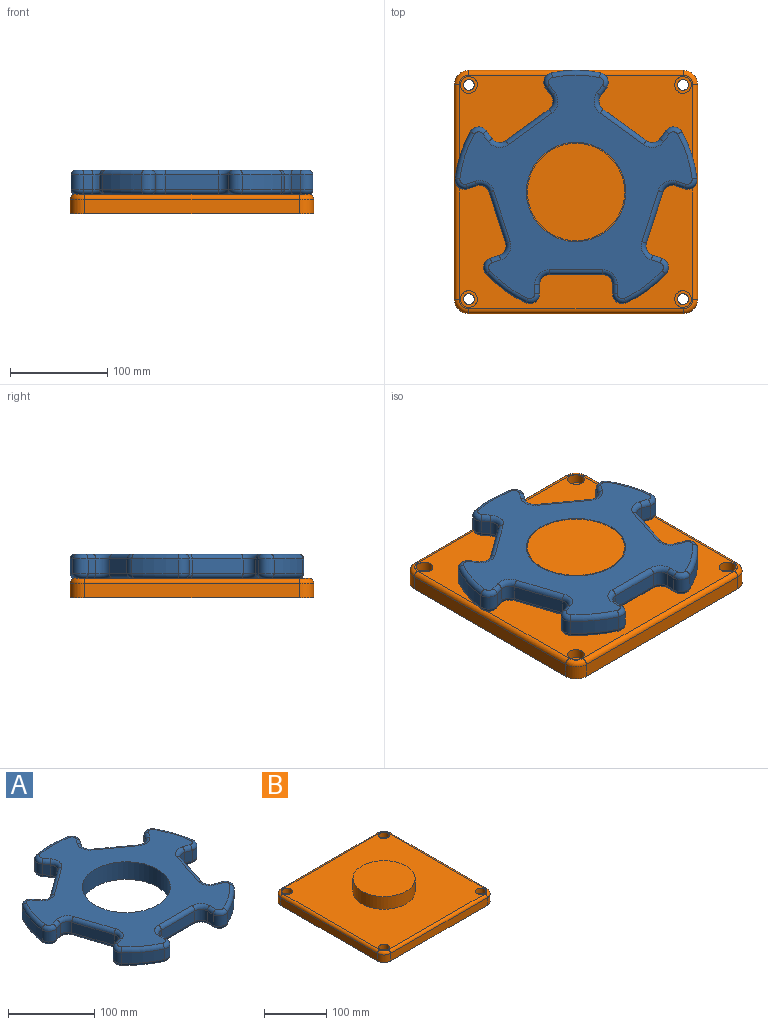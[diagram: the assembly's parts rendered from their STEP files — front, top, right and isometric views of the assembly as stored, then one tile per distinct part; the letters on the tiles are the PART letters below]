
ASSEMBLY  parts=2 mates=1
PART A: 123 faces, bbox 268.9x258.5x25 mm
  f0: plane 238.57x229.73mm, normal (0,0,1), area 21505.7mm2, adj f6,f43,f44,f45,f46,f47,f48,f49
  f1: plane 238.57x229.73mm, normal (0,0,-1), area 21505.7mm2, adj f6,f83,f84,f85,f86,f87,f88,f89
  f2: cylinder r=125mm len=40.68mm, axis (0,0,-1), area 759.5mm2, adj f13,f42,f51,f91
  f3: cylinder r=125mm len=47.82mm, axis (0,0,-1), area 759.5mm2, adj f35,f41,f67,f107
  f4: cylinder r=125mm len=50.29mm, axis (0,0,-1), area 759.5mm2, adj f28,f34,f82,f122
  f5: cylinder r=125mm len=47.82mm, axis (0,0,-1), area 759.5mm2, adj f21,f27,f66,f106
  f6: cylinder r=51mm len=102mm, axis (0,0,-1), area 8011.1mm2, adj f0,f1
  f7: cylinder r=125mm len=40.68mm, axis (0,0,-1), area 759.5mm2, adj f14,f20,f50,f90
  f8: plane 15x9.73mm, normal (-1,0,0), area 146mm2, adj f11,f14,f46,f86
  f9: plane 55x15mm, normal (0,-1,0), area 825mm2, adj f11,f12,f43,f83
  f10: plane 15x9.73mm, normal (1,0,0), area 146mm2, adj f12,f13,f47,f87
  f11: cylinder r=10mm len=15mm, axis (0,0,-1), area 235.6mm2, adj f8,f9,f44,f84
  f12: cylinder r=10mm len=15mm, axis (0,0,-1), area 235.6mm2, adj f9,f10,f45,f85
  f13: cylinder r=10mm len=15mm, axis (0,0,-1), area 299.5mm2, adj f2,f10,f49,f89
  f14: cylinder r=10mm len=15mm, axis (0,0,-1), area 299.5mm2, adj f7,f8,f48,f88
  f15: plane 15x9.26mm, normal (-0.31,-0.95,0), area 146mm2, adj f18,f21,f62,f102
  f16: plane 52.31x17mm, normal (0.95,-0.31,0), area 825mm2, adj f18,f19,f58,f98
  f17: plane 15x9.26mm, normal (0.31,0.95,0), area 146mm2, adj f19,f20,f54,f94
  f18: cylinder r=10mm len=15mm, axis (0,0,-1), area 235.6mm2, adj f15,f16,f60,f100
  f19: cylinder r=10mm len=15mm, axis (0,0,-1), area 235.6mm2, adj f16,f17,f56,f96
  f20: cylinder r=10mm len=16.25mm, axis (0,0,-1), area 299.5mm2, adj f7,f17,f52,f92
  f21: cylinder r=10mm len=15mm, axis (0,0,-1), area 299.5mm2, adj f5,f15,f64,f104
  f22: plane 15x7.87mm, normal (0.81,-0.59,0), area 146mm2, adj f25,f28,f78,f118
  f23: plane 44.5x32.33mm, normal (0.59,0.81,0), area 825mm2, adj f25,f26,f74,f114
  f24: plane 15x7.87mm, normal (-0.81,0.59,0), area 146mm2, adj f26,f27,f70,f110
  f25: cylinder r=10mm len=15mm, axis (0,0,-1), area 235.6mm2, adj f22,f23,f76,f116
  f26: cylinder r=10mm len=15mm, axis (0,0,-1), area 235.6mm2, adj f23,f24,f72,f112
  f27: cylinder r=10mm len=16.78mm, axis (0,0,-1), area 299.5mm2, adj f5,f24,f68,f108
  f28: cylinder r=10mm len=15.67mm, axis (0,0,-1), area 299.5mm2, adj f4,f22,f80,f120
  f29: plane 15x7.87mm, normal (0.81,0.59,0), area 146mm2, adj f32,f35,f71,f111
  f30: plane 44.5x32.33mm, normal (-0.59,0.81,0), area 825mm2, adj f32,f33,f75,f115
  f31: plane 15x7.87mm, normal (-0.81,-0.59,0), area 146mm2, adj f33,f34,f79,f119
  f32: cylinder r=10mm len=15mm, axis (0,0,-1), area 235.6mm2, adj f29,f30,f73,f113
  f33: cylinder r=10mm len=15mm, axis (0,0,-1), area 235.6mm2, adj f30,f31,f77,f117
  f34: cylinder r=10mm len=15.67mm, axis (0,0,-1), area 299.5mm2, adj f4,f31,f81,f121
  f35: cylinder r=10mm len=16.78mm, axis (0,0,-1), area 299.5mm2, adj f3,f29,f69,f109
  f36: plane 15x9.26mm, normal (-0.31,0.95,0), area 146mm2, adj f39,f42,f55,f95
  f37: plane 52.31x17mm, normal (-0.95,-0.31,0), area 825mm2, adj f39,f40,f59,f99
  f38: plane 15x9.26mm, normal (0.31,-0.95,0), area 146mm2, adj f40,f41,f63,f103
  f39: cylinder r=10mm len=15mm, axis (0,0,-1), area 235.6mm2, adj f36,f37,f57,f97
  f40: cylinder r=10mm len=15mm, axis (0,0,-1), area 235.6mm2, adj f37,f38,f61,f101
  f41: cylinder r=10mm len=15mm, axis (0,0,-1), area 299.5mm2, adj f3,f38,f65,f105
  f42: cylinder r=10mm len=16.25mm, axis (0,0,-1), area 299.5mm2, adj f2,f36,f53,f93
  f43: cylinder r=5mm len=55mm, axis (1,0,0), area 432mm2, adj f0,f9,f44,f45
  f44: torus R=15mm, axis (0,0,1), area 145.8mm2, adj f0,f11,f43,f46
  f45: torus R=15mm, axis (0,0,1), area 145.8mm2, adj f0,f12,f43,f47
  f46: cylinder r=5mm len=9.73mm, axis (0,-1,0), area 76.4mm2, adj f0,f8,f44,f48
  f47: cylinder r=5mm len=9.73mm, axis (0,1,0), area 76.4mm2, adj f0,f10,f45,f49
  f48: torus R=5mm, axis (0,0,1), area 128.3mm2, adj f0,f14,f46,f50
  f49: torus R=5mm, axis (0,0,1), area 128.3mm2, adj f0,f13,f47,f51
  f50: torus R=120mm, axis (0,0,1), area 391.9mm2, adj f0,f7,f48,f52
  f51: torus R=120mm, axis (0,0,1), area 391.9mm2, adj f0,f2,f49,f53
  f52: torus R=5mm, axis (0,0,1), area 128.3mm2, adj f0,f20,f50,f54
  f53: torus R=5mm, axis (0,0,1), area 128.3mm2, adj f0,f42,f51,f55
  f54: cylinder r=5mm len=10.8mm, axis (-0.95,0.31,0), area 76.4mm2, adj f0,f17,f52,f56
  f55: cylinder r=5mm len=10.8mm, axis (-0.95,-0.31,0), area 76.4mm2, adj f0,f36,f53,f57
  f56: torus R=15mm, axis (0,0,1), area 145.8mm2, adj f0,f19,f54,f58
  f57: torus R=15mm, axis (0,0,1), area 145.8mm2, adj f0,f39,f55,f59
  f58: cylinder r=5mm len=53.85mm, axis (0.31,0.95,0), area 432mm2, adj f0,f16,f56,f60
  f59: cylinder r=5mm len=53.85mm, axis (0.31,-0.95,0), area 432mm2, adj f0,f37,f57,f61
  f60: torus R=15mm, axis (0,0,1), area 145.8mm2, adj f0,f18,f58,f62
  f61: torus R=15mm, axis (0,0,1), area 145.8mm2, adj f0,f40,f59,f63
  f62: cylinder r=5mm len=10.8mm, axis (0.95,-0.31,0), area 76.4mm2, adj f0,f15,f60,f64
  f63: cylinder r=5mm len=10.8mm, axis (0.95,0.31,0), area 76.4mm2, adj f0,f38,f61,f65
  f64: torus R=5mm, axis (0,0,1), area 128.3mm2, adj f0,f21,f62,f66
  f65: torus R=5mm, axis (0,0,1), area 128.3mm2, adj f0,f41,f63,f67
  f66: torus R=120mm, axis (0,0,1), area 391.9mm2, adj f0,f5,f64,f68
  f67: torus R=120mm, axis (0,0,1), area 391.9mm2, adj f0,f3,f65,f69
  f68: torus R=5mm, axis (0,0,1), area 128.3mm2, adj f0,f27,f66,f70
  f69: torus R=5mm, axis (0,0,1), area 128.3mm2, adj f0,f35,f67,f71
  f70: cylinder r=5mm len=10.81mm, axis (-0.59,-0.81,0), area 76.4mm2, adj f0,f24,f68,f72
  f71: cylinder r=5mm len=10.81mm, axis (-0.59,0.81,0), area 76.4mm2, adj f0,f29,f69,f73
  f72: torus R=15mm, axis (0,0,1), area 145.8mm2, adj f0,f26,f70,f74
  f73: torus R=15mm, axis (0,0,1), area 145.8mm2, adj f0,f32,f71,f75
  f74: cylinder r=5mm len=47.44mm, axis (-0.81,0.59,0), area 432mm2, adj f0,f23,f72,f76
  f75: cylinder r=5mm len=47.44mm, axis (-0.81,-0.59,0), area 432mm2, adj f0,f30,f73,f77
  f76: torus R=15mm, axis (0,0,1), area 145.8mm2, adj f0,f25,f74,f78
  f77: torus R=15mm, axis (0,0,1), area 145.8mm2, adj f0,f33,f75,f79
  f78: cylinder r=5mm len=10.81mm, axis (0.59,0.81,0), area 76.4mm2, adj f0,f22,f76,f80
  f79: cylinder r=5mm len=10.81mm, axis (0.59,-0.81,0), area 76.4mm2, adj f0,f31,f77,f81
  f80: torus R=5mm, axis (0,0,1), area 128.3mm2, adj f0,f28,f78,f82
  f81: torus R=5mm, axis (0,0,1), area 128.3mm2, adj f0,f34,f79,f82
  f82: torus R=120mm, axis (0,0,1), area 391.9mm2, adj f0,f4,f80,f81
  f83: cylinder r=5mm len=55mm, axis (-1,0,0), area 432mm2, adj f1,f9,f84,f85
  f84: torus R=15mm, axis (0,0,1), area 145.8mm2, adj f1,f11,f83,f86
  f85: torus R=15mm, axis (0,0,1), area 145.8mm2, adj f1,f12,f83,f87
  f86: cylinder r=5mm len=9.73mm, axis (0,1,0), area 76.4mm2, adj f1,f8,f84,f88
  f87: cylinder r=5mm len=9.73mm, axis (0,-1,0), area 76.4mm2, adj f1,f10,f85,f89
  f88: torus R=5mm, axis (0,0,1), area 128.3mm2, adj f1,f14,f86,f90
  f89: torus R=5mm, axis (0,0,1), area 128.3mm2, adj f1,f13,f87,f91
  f90: torus R=120mm, axis (0,0,1), area 391.9mm2, adj f1,f7,f88,f92
  f91: torus R=120mm, axis (0,0,1), area 391.9mm2, adj f1,f2,f89,f93
  f92: torus R=5mm, axis (0,0,1), area 128.3mm2, adj f1,f20,f90,f94
  f93: torus R=5mm, axis (0,0,1), area 128.3mm2, adj f1,f42,f91,f95
  f94: cylinder r=5mm len=10.8mm, axis (0.95,-0.31,0), area 76.4mm2, adj f1,f17,f92,f96
  f95: cylinder r=5mm len=10.8mm, axis (0.95,0.31,0), area 76.4mm2, adj f1,f36,f93,f97
  f96: torus R=15mm, axis (0,0,1), area 145.8mm2, adj f1,f19,f94,f98
  f97: torus R=15mm, axis (0,0,1), area 145.8mm2, adj f1,f39,f95,f99
  f98: cylinder r=5mm len=53.85mm, axis (-0.31,-0.95,0), area 432mm2, adj f1,f16,f96,f100
  f99: cylinder r=5mm len=53.85mm, axis (-0.31,0.95,0), area 432mm2, adj f1,f37,f97,f101
  f100: torus R=15mm, axis (0,0,1), area 145.8mm2, adj f1,f18,f98,f102
  f101: torus R=15mm, axis (0,0,1), area 145.8mm2, adj f1,f40,f99,f103
  f102: cylinder r=5mm len=10.8mm, axis (-0.95,0.31,0), area 76.4mm2, adj f1,f15,f100,f104
  f103: cylinder r=5mm len=10.8mm, axis (-0.95,-0.31,0), area 76.4mm2, adj f1,f38,f101,f105
  f104: torus R=5mm, axis (0,0,1), area 128.3mm2, adj f1,f21,f102,f106
  f105: torus R=5mm, axis (0,0,1), area 128.3mm2, adj f1,f41,f103,f107
  f106: torus R=120mm, axis (0,0,1), area 391.9mm2, adj f1,f5,f104,f108
  f107: torus R=120mm, axis (0,0,1), area 391.9mm2, adj f1,f3,f105,f109
  f108: torus R=5mm, axis (0,0,1), area 128.3mm2, adj f1,f27,f106,f110
  f109: torus R=5mm, axis (0,0,1), area 128.3mm2, adj f1,f35,f107,f111
  f110: cylinder r=5mm len=10.81mm, axis (0.59,0.81,0), area 76.4mm2, adj f1,f24,f108,f112
  f111: cylinder r=5mm len=10.81mm, axis (0.59,-0.81,0), area 76.4mm2, adj f1,f29,f109,f113
  f112: torus R=15mm, axis (0,0,1), area 145.8mm2, adj f1,f26,f110,f114
  f113: torus R=15mm, axis (0,0,1), area 145.8mm2, adj f1,f32,f111,f115
  f114: cylinder r=5mm len=47.44mm, axis (0.81,-0.59,0), area 432mm2, adj f1,f23,f112,f116
  f115: cylinder r=5mm len=47.44mm, axis (0.81,0.59,0), area 432mm2, adj f1,f30,f113,f117
  f116: torus R=15mm, axis (0,0,1), area 145.8mm2, adj f1,f25,f114,f118
  f117: torus R=15mm, axis (0,0,1), area 145.8mm2, adj f1,f33,f115,f119
  f118: cylinder r=5mm len=10.81mm, axis (-0.59,-0.81,0), area 76.4mm2, adj f1,f22,f116,f120
  f119: cylinder r=5mm len=10.81mm, axis (-0.59,0.81,0), area 76.4mm2, adj f1,f31,f117,f121
  f120: torus R=5mm, axis (0,0,1), area 128.3mm2, adj f1,f28,f118,f122
  f121: torus R=5mm, axis (0,0,1), area 128.3mm2, adj f1,f34,f119,f122
  f122: torus R=120mm, axis (0,0,1), area 391.9mm2, adj f1,f4,f120,f121
PART B: 32 faces, bbox 252.5x252.5x45 mm
  f0: plane 220x15mm, normal (1,0,0), area 3300mm2, adj f5,f8,f11,f27
  f1: plane 220x15mm, normal (0,1,0), area 3300mm2, adj f5,f8,f9,f31
  f2: plane 220x15mm, normal (-1,0,0), area 3300mm2, adj f5,f9,f10,f28
  f3: plane 220x15mm, normal (0,-1,0), area 3300mm2, adj f5,f10,f11,f24
  f4: plane 240x240mm, normal (0,0,1), area 48725.4mm2, adj f6,f14,f17,f20,f23,f24,f25,f26
  f5: plane 250x250mm, normal (0,0,-1), area 61926.7mm2, adj f0,f1,f2,f3,f8,f9,f10,f11
  f6: cylinder r=50mm len=100mm, axis (0,0,-1), area 7854mm2, adj f4,f7
  f7: plane 100x100mm, normal (0,0,1), area 7854mm2, adj f6
  f8: cylinder r=15mm len=15mm, axis (0,0,-1), area 353.4mm2, adj f0,f1,f5,f29
  f9: cylinder r=15mm len=15mm, axis (0,0,1), area 353.4mm2, adj f1,f2,f5,f30
  f10: cylinder r=15mm len=15mm, axis (0,0,-1), area 353.4mm2, adj f2,f3,f5,f26
  f11: cylinder r=15mm len=15mm, axis (0,0,1), area 353.4mm2, adj f0,f3,f5,f25
  f12: cylinder r=5.5mm len=11mm, axis (0,0,1), area 345.6mm2, adj f5,f13
  f13: plane 17.25x17.25mm, normal (0,0,1), area 138.7mm2, adj f12,f14
  f14: cylinder r=8.62mm len=17.25mm, axis (0,0,1), area 541.9mm2, adj f4,f13
  f15: cylinder r=5.5mm len=11mm, axis (0,0,1), area 345.6mm2, adj f5,f16
  f16: plane 17.25x17.25mm, normal (0,0,1), area 138.7mm2, adj f15,f17
  f17: cylinder r=8.62mm len=17.25mm, axis (0,0,1), area 541.9mm2, adj f4,f16
  f18: cylinder r=5.5mm len=11mm, axis (0,0,1), area 345.6mm2, adj f5,f19
  f19: plane 17.25x17.25mm, normal (0,0,1), area 138.7mm2, adj f18,f20
  f20: cylinder r=8.62mm len=17.25mm, axis (0,0,1), area 541.9mm2, adj f4,f19
  f21: cylinder r=5.5mm len=11mm, axis (0,0,1), area 345.6mm2, adj f5,f22
  f22: plane 17.25x17.25mm, normal (0,0,1), area 138.7mm2, adj f21,f23
  f23: cylinder r=8.62mm len=17.25mm, axis (0,0,1), area 541.9mm2, adj f4,f22
  f24: cylinder r=5mm len=220mm, axis (-1,0,0), area 1727.9mm2, adj f3,f4,f25,f26
  f25: torus R=10mm, axis (0,0,1), area 162.6mm2, adj f4,f11,f24,f27
  f26: torus R=10mm, axis (0,0,1), area 162.6mm2, adj f4,f10,f24,f28
  f27: cylinder r=5mm len=220mm, axis (0,-1,0), area 1727.9mm2, adj f0,f4,f25,f29
  f28: cylinder r=5mm len=220mm, axis (0,1,0), area 1727.9mm2, adj f2,f4,f26,f30
  f29: torus R=10mm, axis (0,0,1), area 162.6mm2, adj f4,f8,f27,f31
  f30: torus R=10mm, axis (0,0,1), area 162.6mm2, adj f4,f9,f28,f31
  f31: cylinder r=5mm len=220mm, axis (1,0,0), area 1727.9mm2, adj f1,f4,f29,f30
PLACE A at identity
PLACE B at identity fixed
MATE revolute A.f2 <-> B.f6  axis (0,0,1) through (0,0,45)mm
